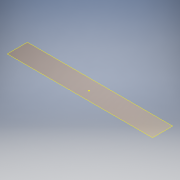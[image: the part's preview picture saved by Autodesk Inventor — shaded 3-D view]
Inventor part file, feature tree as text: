
AUTODESK INVENTOR PART (.ipt)
format: ipt  version: 2016 (Build 200138000, 138)  size: 79,360 bytes
history: native  units: mm
features: plane x1, sketch x1, reference x1
ambient origin geometry x8: Origin, YZ Plane, XZ Plane, XY Plane, X Axis, Y Axis, Z Axis, Center Point
feature tree (3):
  plane  "Work Plane1"
  sketch  "Sketch1"
  reference  "Reference1"
